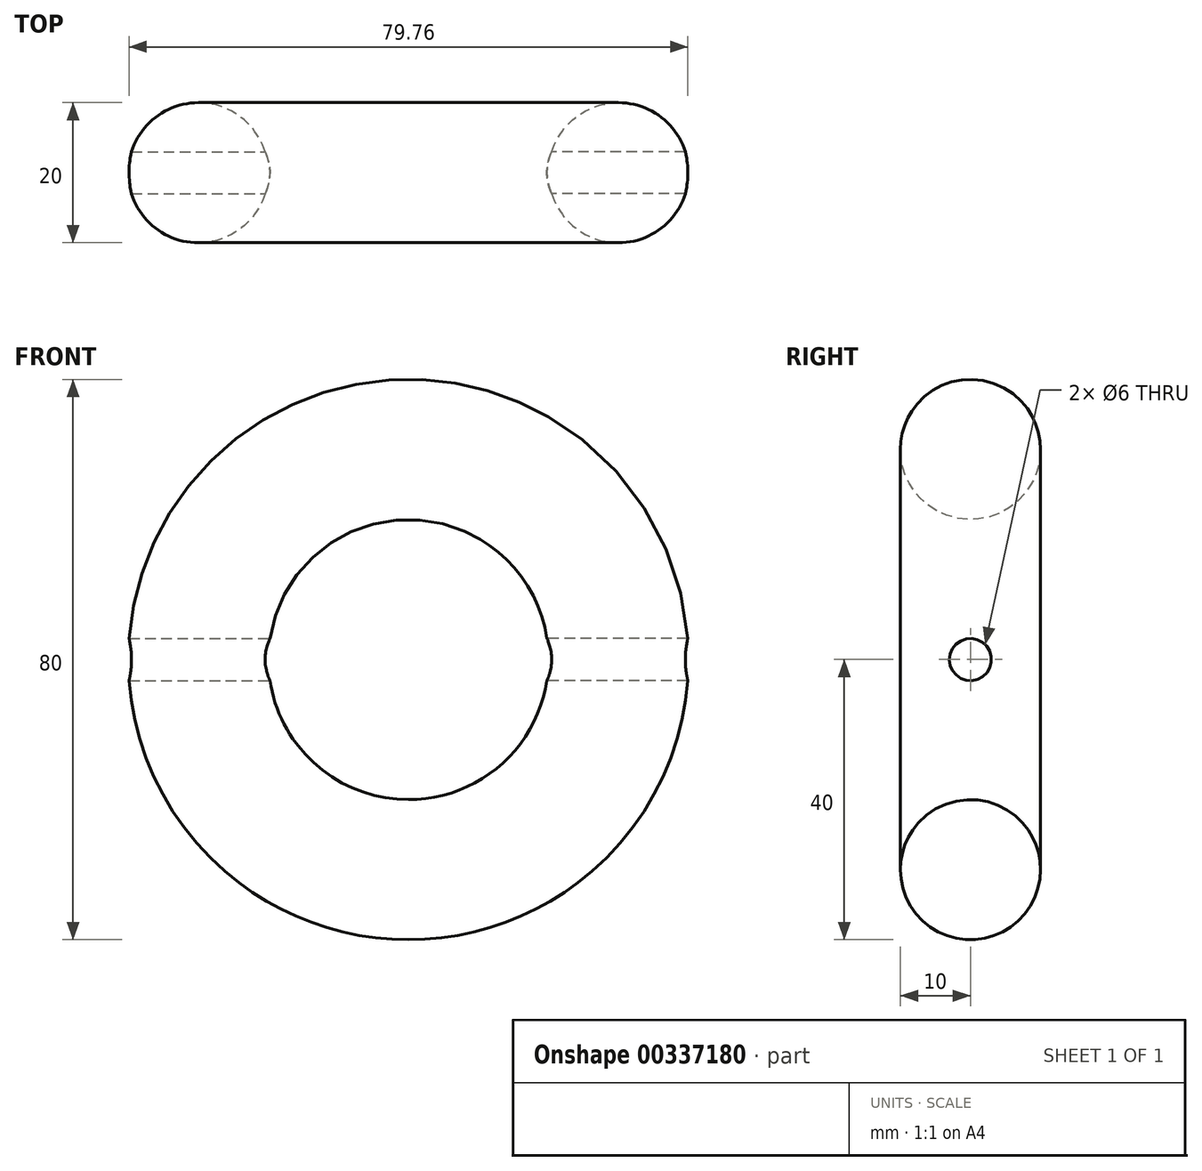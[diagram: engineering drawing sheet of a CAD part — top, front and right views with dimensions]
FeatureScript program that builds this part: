
annotation { "Feature Type Name" : "Feature", "Feature Type Description" : "" }
export const myFeature = defineFeature(function(context is Context, id is Id, definition is map)
    precondition{}
    {
        {
            var Q0;
            Q0=qCreatedBy(makeId("Front.planeOp"),FACE);
            var sketch = newSketch(context, id + "F0", { "sketchPlane" : qUnion([Q0])});
            skArc(sketch, "E0", {"start": v(0, 40) * mm, "mid": v(40, 0) * mm, "end": v(0, -40) * mm});
            skArc(sketch, "E1", {"start": v(0, -20) * mm, "mid": v(20, 0) * mm, "end": v(0, 20) * mm});
            skLineSegment(sketch, "E2", {"start": v(0, 40) * mm, "end": v(0, 20) * mm});
            skLineSegment(sketch, "E3", {"start": v(0, -20) * mm, "end": v(0, -40) * mm});
            skCircle(sketch, "E4", {"center": v(0, 0) * mm, "radius": 40 * mm});
            skCircle(sketch, "E5", {"center": v(0, 0) * mm, "radius": 20 * mm});
            skSolve(sketch);
        }
        {
            var Q0;
            Q0=qCreatedBy(makeId("Top.planeOp"),FACE);
            var sketch = newSketch(context, id + "F1", { "sketchPlane" : qUnion([Q0])});
            skCircle(sketch, "E6", {"center": v(30, -10) * mm, "radius": 10 * mm});
            skCircle(sketch, "E7", {"center": v(-30, -10) * mm, "radius": 10 * mm});
            skLineSegment(sketch, "E8", {"start": v(0, 0) * mm, "end": v(0, -76.75) * mm});
            skSolve(sketch);
        }
        {
            var Q0;
            Q0=makeQuery(id+"F1.imprint","IMPRINT",FACE,{"disambiguationData":[TD([[makeQuery(id+"F1.imprint","IMPRINT",EDGE,{"derivedFrom":sQuery(id+"F1.wireOp",EDGE,"E6")}),1.0]])]});
            var Q1;
            Q1=sQuery(id+"F1.wireOp",EDGE,"E6");
            var Q2;
            Q2=sQuery(id+"F1.wireOp",EDGE,"E8");
            revolve(context, id + "F2", {"entities" : qUnion([Q0]), "surfaceEntities" : qUnion([Q1]), "axis" : qUnion([Q2]), "revolveType" : RevolveType.FULL});
        }
        {
            var Q0;
            Q0=qCreatedBy(makeId("Right.planeOp"),FACE);
            var sketch = newSketch(context, id + "F3", { "sketchPlane" : qUnion([Q0])});
            skCircle(sketch, "E9", {"center": v(-10, 0) * mm, "radius": 3 * mm});
            skSolve(sketch);
        }
        {
            var Q0;
            Q0 = qSketchRegion(id + "F3", true);
            extrude(context, id + "F4", {"entities" : qUnion([Q0]), "operationType" : NewBodyOperationType.REMOVE, "endBound" : BoundingType.THROUGH_ALL, "depth" : 25 * mm});
        }
        {
            var Q0;
            Q0=qCreatedBy(makeId("Right.planeOp"),FACE);
            var sketch = newSketch(context, id + "F5", { "sketchPlane" : qUnion([Q0])});
            skCircle(sketch, "E10", {"center": v(-10, 0) * mm, "radius": 3 * mm});
            skSolve(sketch);
        }
        {
            var Q0;
            Q0 = qSketchRegion(id + "F5", true);
            extrude(context, id + "F6", {"entities" : qUnion([Q0]), "operationType" : NewBodyOperationType.REMOVE, "endBound" : BoundingType.THROUGH_ALL, "oppositeDirection" : true, "depth" : 25 * mm});
        }
    });
